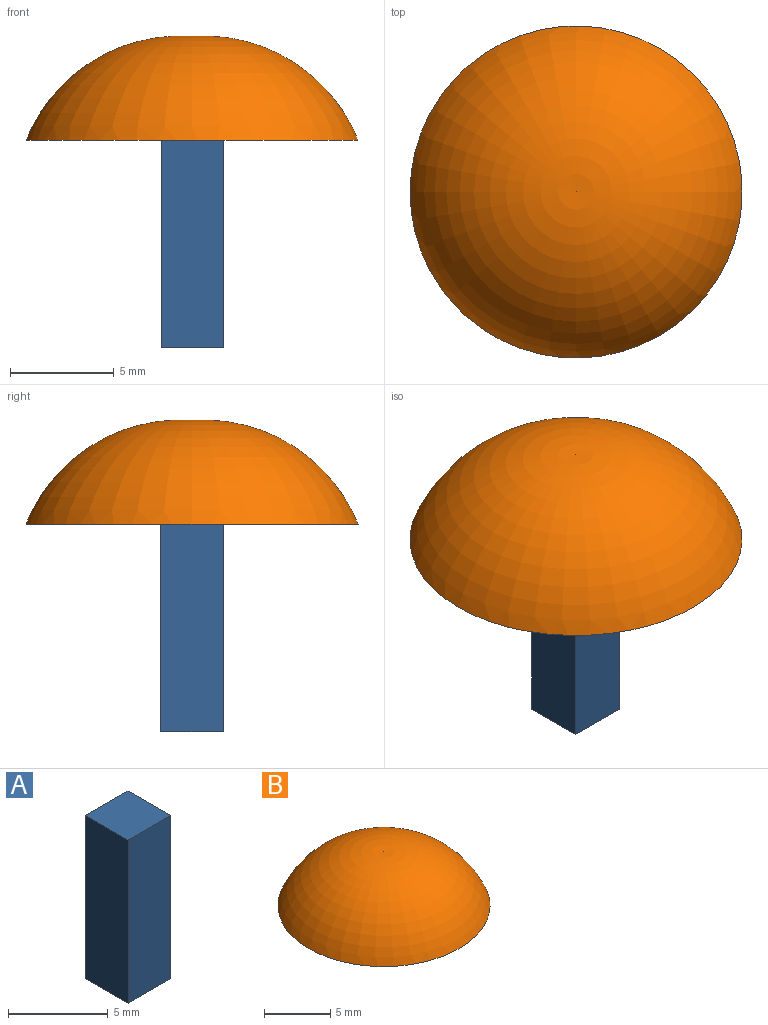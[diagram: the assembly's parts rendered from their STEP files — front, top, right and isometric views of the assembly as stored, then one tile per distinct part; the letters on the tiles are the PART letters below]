
ASSEMBLY  parts=2 mates=1
PART A: 6 faces, bbox 3x3x10 mm
  f0: plane 10x3mm, normal (0,-1,0), area 30mm2, adj f1,f3,f4,f5
  f1: plane 10x3mm, normal (1,0,0), area 30mm2, adj f0,f2,f4,f5
  f2: plane 10x3mm, normal (0,1,0), area 30mm2, adj f1,f3,f4,f5
  f3: plane 10x3mm, normal (-1,0,0), area 30mm2, adj f0,f2,f4,f5
  f4: plane 3x3mm, normal (0,0,1), area 9mm2, adj f0,f1,f2,f3
  f5: plane 3x3mm, normal (0,0,-1), area 9mm2, adj f0,f1,f2,f3
PART B: 2 faces, bbox 16x16x5 mm
  f0: plane 16x16mm, normal (0,0,-1), area 201.1mm2, adj f1
  f1: torus R=0.58mm, axis (0,0,-1), area 287.8mm2, adj f0
PLACE A t=(-5.4,0.92,-15.58)mm
PLACE B t=(-6.9,2.42,-5.58)mm
MATE fastened B.f1 <-> A.f4  axis (0,0,-1) through (-6.9,2.42,-5.58)mm
